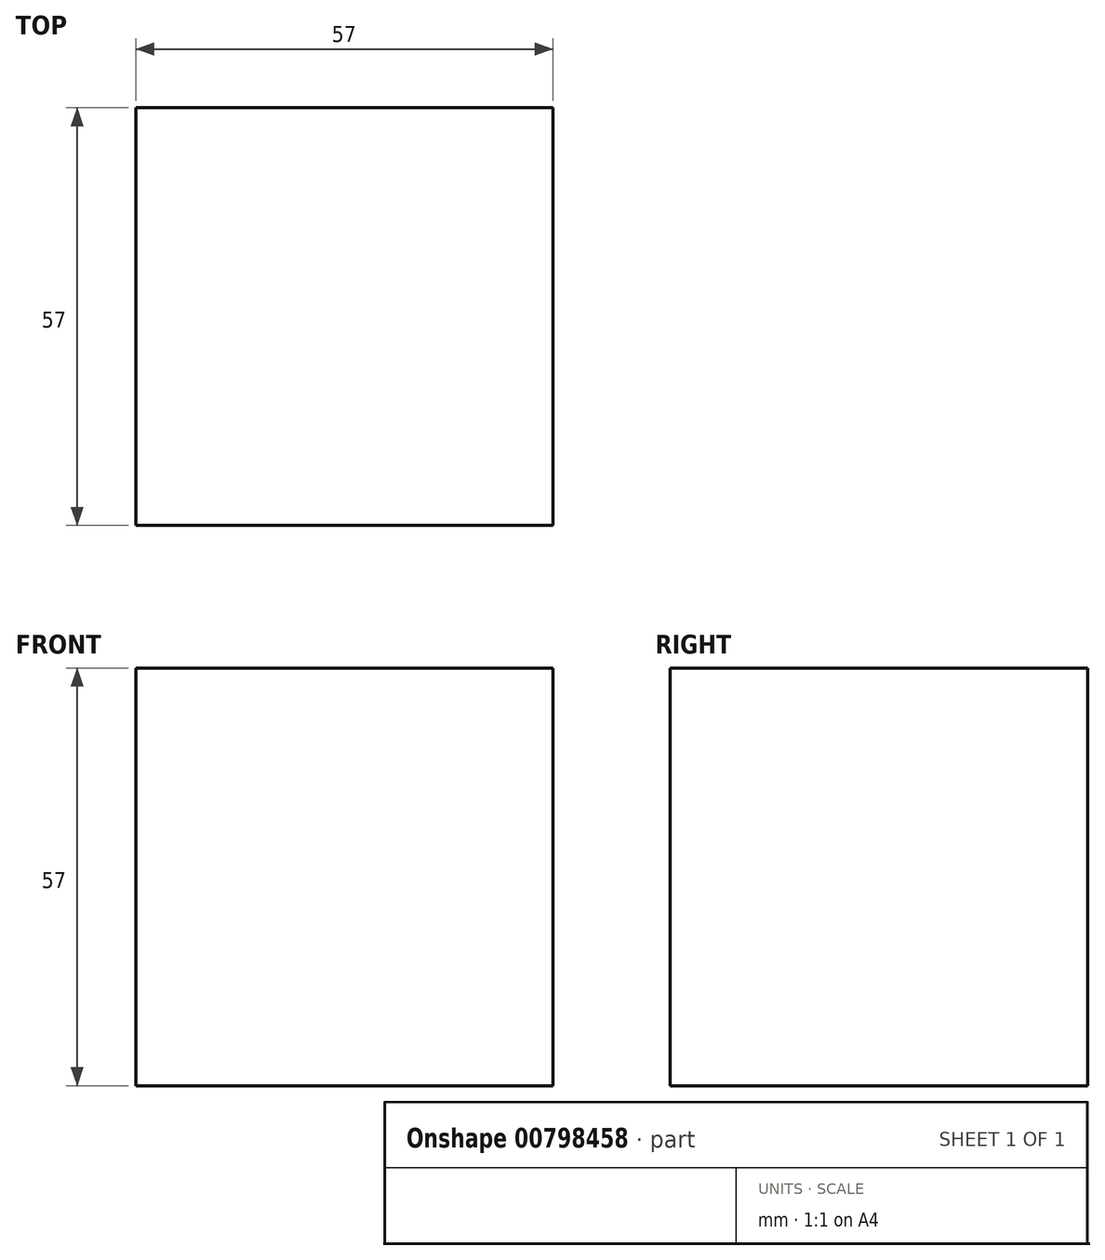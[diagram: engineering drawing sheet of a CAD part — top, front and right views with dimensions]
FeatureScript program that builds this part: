
annotation { "Feature Type Name" : "Feature", "Feature Type Description" : "" }
export const myFeature = defineFeature(function(context is Context, id is Id, definition is map)
    precondition{}
    {
        {
            var Q0;
            Q0=qCreatedBy(makeId("Top.planeOp"),FACE);
            var sketch = newSketch(context, id + "F0", { "sketchPlane" : qUnion([Q0])});
            skPoint(sketch, "E0.middle", {"position": v(0, 0) * mm});
            skLineSegment(sketch, "E1.bottom", {"start": v(28.5, -28.5) * mm, "end": v(-28.5, -28.5) * mm});
            skLineSegment(sketch, "E1.top", {"start": v(28.5, 28.5) * mm, "end": v(-28.5, 28.5) * mm});
            skLineSegment(sketch, "E1.left", {"start": v(28.5, -28.5) * mm, "end": v(28.5, 28.5) * mm});
            skLineSegment(sketch, "E1.right", {"start": v(-28.5, -28.5) * mm, "end": v(-28.5, 28.5) * mm});
            skSolve(sketch);
        }
        {
            var Q0;
            Q0=makeQuery(id+"F0.imprint","IMPRINT",FACE,{"disambiguationData":[TD([[makeQuery(id+"F0.imprint","IMPRINT",EDGE,{"derivedFrom":sQuery(id+"F0.wireOp",EDGE,"E1.bottom")}),-1.0]])]});
            extrude(context, id + "F1", {"entities" : qUnion([Q0]), "depth" : 57 * mm, "offsetDistance" : 25.4 * mm});
        }
    });
